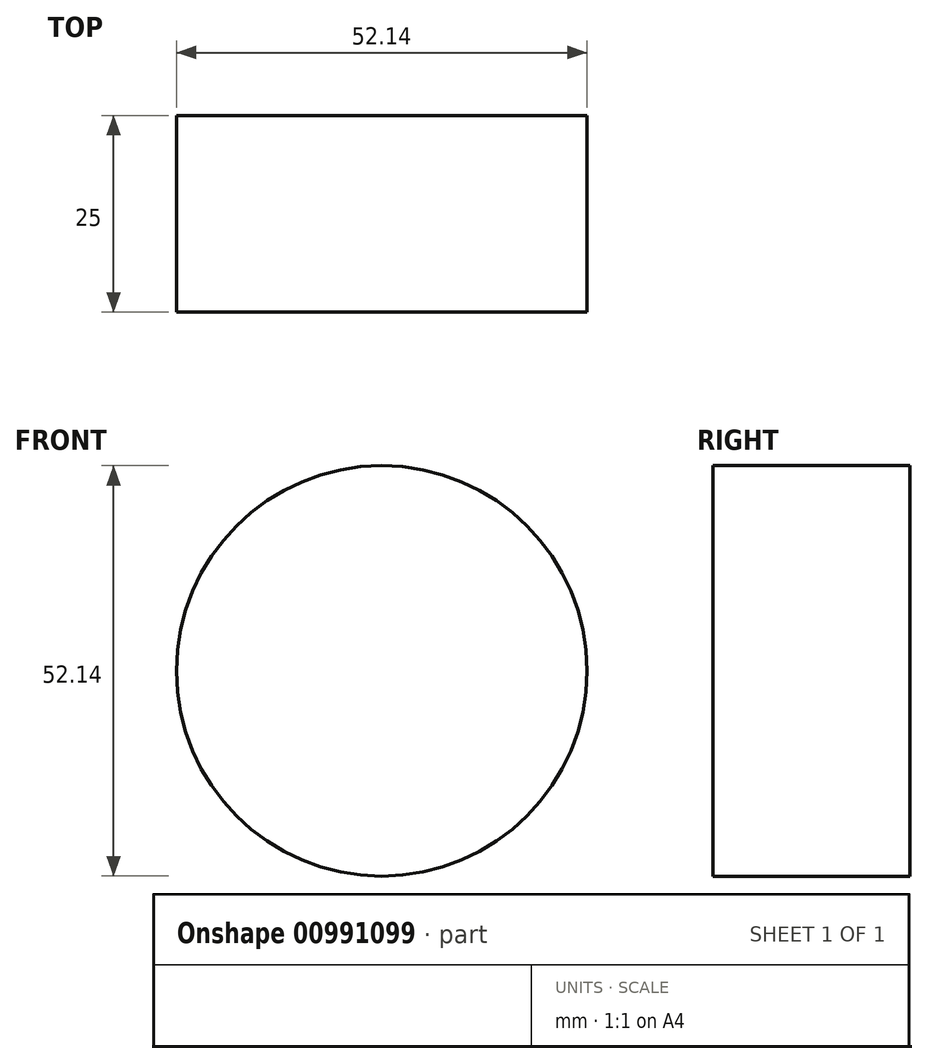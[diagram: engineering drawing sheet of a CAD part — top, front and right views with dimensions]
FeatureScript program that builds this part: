
annotation { "Feature Type Name" : "Feature", "Feature Type Description" : "" }
export const myFeature = defineFeature(function(context is Context, id is Id, definition is map)
    precondition{}
    {
        {
            var Q0;
            Q0=qCreatedBy(makeId("Front.planeOp"),FACE);
            var sketch = newSketch(context, id + "F0", { "sketchPlane" : qUnion([Q0])});
            skCircle(sketch, "E0", {"center": v(0, 0) * mm, "radius": 26.07 * mm});
            skSolve(sketch);
        }
        {
            var Q0;
            Q0=makeQuery(id+"F0.imprint","IMPRINT",FACE,{"disambiguationData":[TD([[makeQuery(id+"F0.imprint","IMPRINT",EDGE,{"derivedFrom":sQuery(id+"F0.wireOp",EDGE,"E0")}),1.0]])]});
            extrude(context, id + "F1", {"entities" : qUnion([Q0]), "depth" : 25 * mm, "offsetDistance" : 25 * mm});
        }
    });
